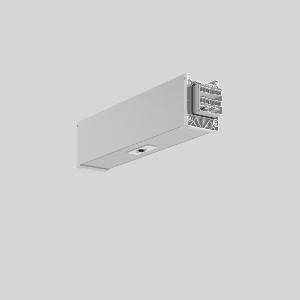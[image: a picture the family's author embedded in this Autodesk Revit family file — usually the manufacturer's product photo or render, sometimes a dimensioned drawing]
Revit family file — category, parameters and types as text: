
# Revit family: linedo_sensormodule_2-5_m_9503s1_000_400_000_66e4
name_source: partatom
category: Lighting Fixtures
units: mm (PartAtom-declared; Revit-internal decimal feet)

## family parameters
Cut with Voids When Loaded = No
Host = Face
Light Source = No
Part Type = Normal
Room Calculation Point = No
Round Connector Dimension = Use Diameter
Shared = No

## types (1)
- LINEDO Sensormodule 2-5 m
    Apparent Load = 0 VA
    Default Elevation = 1800 mm
    Description = Series: LINEDO
Module including Passive Infrared (PIR) sensor for movement and ambient light. System profile made of aluminium extrusion profile, anodised. Simple, tool-free installation of system profiles using separate accessories for cable, chain or ceiling suspension. Tool-free connection and mechanical connectors to secure. 14-poles LINEDO connector (5 x 2.5 mm² / 9 x 1.5 mm²) for additional applications in light management or for the integration of emergency lighting. Phase can be set via patended bridge without opening the luminaire. Pre-assembled connector for DALI line. Light and movement sensor: Housing of non-flammable, halogen-free plastic (polycarbonate). Presence detection with passive IR element. Presence detection range adjustable via integrated shutters between 40° and 90°. Detection range: 6 m. Light sensor range: 20-800 lx (measured at the sensor). Function display with two-colour LED. Installation height: 2-5 m. Example of use: Monitoring of low ceiling rooms and rack storage where the installation height is normal. Please order supply module, connection and mounting accessories separately. 
Colour: anodised aluminium
Length: 330 mm
Width: 58 mm
Height: 76 mm
Weight: 770 g
Type of Installation: Recessed mounting
    Height = 77 mm
    Lamp = 0 x
    Length = 331 mm
    Luminous efficacy = 0 lm/W
    Manufacturer = RZB
    ModVariant = No
    Model = 9503S1.000.400.000
    Mounting Place = Ceiling
    Mounting Type = Surface mounted, Pendant
    Number of Poles = 1
    OnlyDefault = Yes
    Power Factor = 1
    Product Name = LINEDO Sensormodule 2-5 m
    Product group = Surface mounted continuous line luminaire system
    ProductGroupID = 310
    Protection Class = Protection class I
    Protection Degree = IP 20
    RLX_Detail_Level = 1
    RLX_Emergency_Light_Flux = 0 lm
    RLX_Emergency_Type = 0
    RLX_Emergency_Type_DB = No
    RlxData = <blob elided: 22845 chars, md5=8e732ff9>
    Standby Power = 0 W
    System Light Flux = 0 lm
    System Power = 0 W
    Type Comments = Product without accessories
    Type Image = 9503s1.000.400.000.jpg
    URL = http://relux.com
    VarID = ---
    Voltage = 230 V
    Voltage Range = 220-240 V
    Weight = 0.00 kg
    Width = 58 mm

## geometry (parser evidence)
native form markers: Blend x4, Sweep x11
no freeform markers — native parametric forms only
